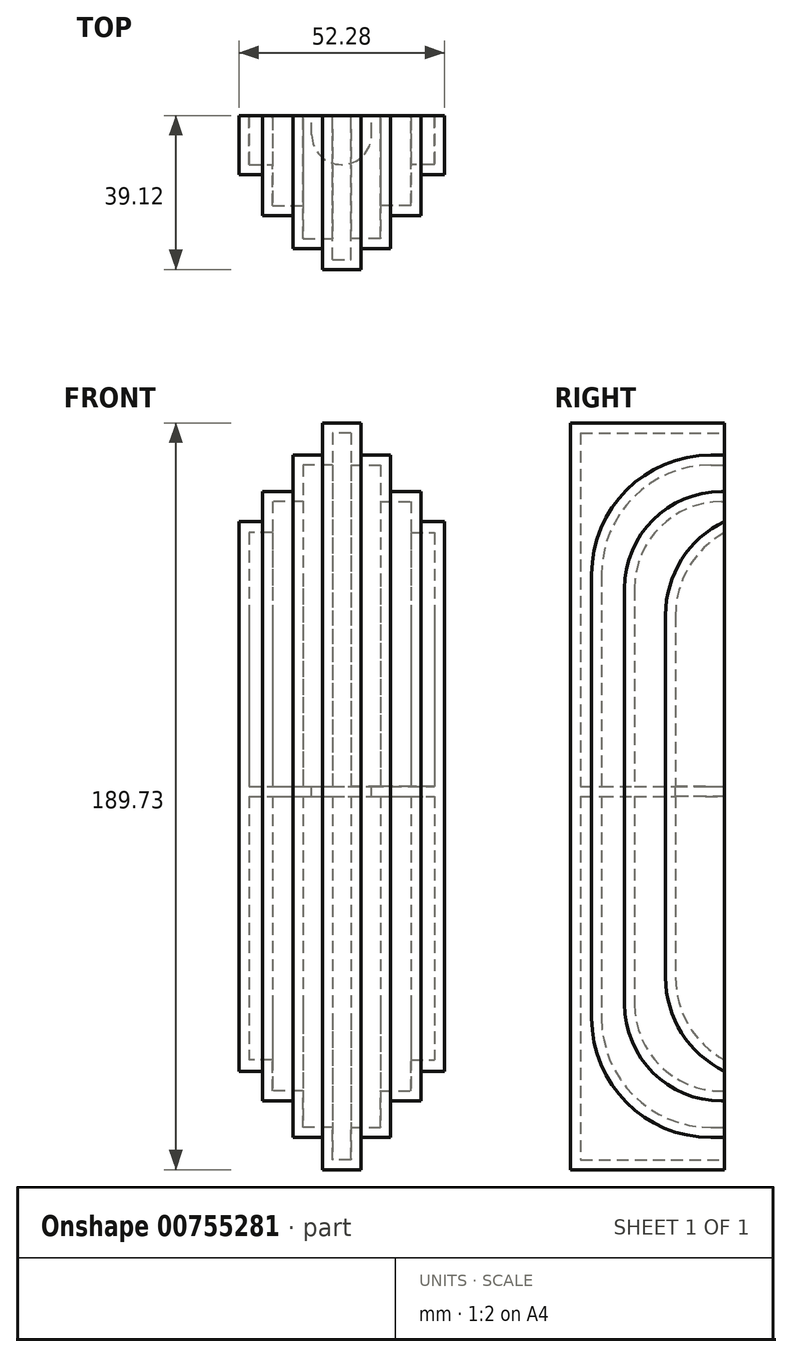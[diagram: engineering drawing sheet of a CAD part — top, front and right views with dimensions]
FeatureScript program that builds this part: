
annotation { "Feature Type Name" : "Feature", "Feature Type Description" : "" }
export const myFeature = defineFeature(function(context is Context, id is Id, definition is map)
    precondition{}
    {
        {
            var Q0;
            Q0=qCreatedBy(makeId("Front.planeOp"),FACE);
            var sketch = newSketch(context, id + "F0", { "sketchPlane" : qUnion([Q0])});
            skLineSegment(sketch, "E0", {"start": v(0, 33.47) * mm, "end": v(-4.86, 33.47) * mm});
            skLineSegment(sketch, "E1", {"start": v(-4.86, 33.47) * mm, "end": v(-4.86, -61.4) * mm});
            skLineSegment(sketch, "E2", {"start": v(-4.86, 25.31) * mm, "end": v(-12.33, 25.31) * mm});
            skLineSegment(sketch, "E3", {"start": v(-12.33, 25.31) * mm, "end": v(-12.33, -61.4) * mm});
            skLineSegment(sketch, "E4", {"start": v(-12.33, 16.06) * mm, "end": v(-20.13, 16.06) * mm});
            skLineSegment(sketch, "E5", {"start": v(-20.13, 16.06) * mm, "end": v(-20.13, -61.4) * mm});
            skLineSegment(sketch, "E6", {"start": v(-20.13, 8.45) * mm, "end": v(-26.14, 8.45) * mm});
            skLineSegment(sketch, "E7", {"start": v(-26.14, 8.45) * mm, "end": v(-26.14, -61.4) * mm});
            skPoint(sketch, "E8.start.orphan", {"position": v(-20.13, -61.4) * mm});
            skLineSegment(sketch, "E9", {"start": v(-26.14, -61.4) * mm, "end": v(-4.86, -61.4) * mm});
            skLineSegment(sketch, "E10.MirrorCS", {"start": v(0, 33.47) * mm, "end": v(4.86, 33.47) * mm});
            skLineSegment(sketch, "E11.MirrorCS", {"start": v(4.86, 33.47) * mm, "end": v(4.86, -61.4) * mm});
            skLineSegment(sketch, "E12.MirrorCS", {"start": v(4.86, 25.31) * mm, "end": v(12.33, 25.31) * mm});
            skLineSegment(sketch, "E13.MirrorCS", {"start": v(12.33, 16.06) * mm, "end": v(20.13, 16.06) * mm});
            skLineSegment(sketch, "E14.MirrorCS", {"start": v(12.33, 25.31) * mm, "end": v(12.33, -61.4) * mm});
            skLineSegment(sketch, "E15.MirrorCS", {"start": v(20.13, 8.45) * mm, "end": v(26.14, 8.45) * mm});
            skLineSegment(sketch, "E16.MirrorCS", {"start": v(26.14, 8.45) * mm, "end": v(26.14, -61.4) * mm});
            skLineSegment(sketch, "E17.MirrorCS", {"start": v(20.13, 16.06) * mm, "end": v(20.13, -61.4) * mm});
            skLineSegment(sketch, "E18.MirrorCS", {"start": v(26.14, -61.4) * mm, "end": v(4.86, -61.4) * mm});
            skLineSegment(sketch, "E19", {"start": v(-4.86, -61.4) * mm, "end": v(4.86, -61.4) * mm});
            skLineSegment(sketch, "E20.MirrorCS", {"start": v(-26.14, -131.24) * mm, "end": v(-26.14, -61.4) * mm});
            skLineSegment(sketch, "E21.MirrorCS", {"start": v(-20.13, -138.85) * mm, "end": v(-20.13, -61.4) * mm});
            skLineSegment(sketch, "E22.MirrorCS", {"start": v(-12.33, -148.1) * mm, "end": v(-12.33, -61.4) * mm});
            skLineSegment(sketch, "E23.MirrorCS", {"start": v(-4.86, -156.26) * mm, "end": v(-4.86, -61.4) * mm});
            skLineSegment(sketch, "E24.MirrorCS", {"start": v(4.86, -156.26) * mm, "end": v(4.86, -61.4) * mm});
            skLineSegment(sketch, "E25.MirrorCS", {"start": v(12.33, -148.1) * mm, "end": v(12.33, -61.4) * mm});
            skLineSegment(sketch, "E26.MirrorCS", {"start": v(20.13, -138.85) * mm, "end": v(20.13, -61.4) * mm});
            skLineSegment(sketch, "E27.MirrorCS", {"start": v(26.14, -131.24) * mm, "end": v(26.14, -61.4) * mm});
            skLineSegment(sketch, "E28.MirrorCS", {"start": v(12.33, -138.85) * mm, "end": v(20.13, -138.85) * mm});
            skLineSegment(sketch, "E29.MirrorCS", {"start": v(20.13, -131.24) * mm, "end": v(26.14, -131.24) * mm});
            skLineSegment(sketch, "E30.MirrorCS", {"start": v(4.86, -148.1) * mm, "end": v(12.33, -148.1) * mm});
            skLineSegment(sketch, "E31.MirrorCS", {"start": v(0, -156.26) * mm, "end": v(4.86, -156.26) * mm});
            skLineSegment(sketch, "E32.MirrorCS", {"start": v(0, -156.26) * mm, "end": v(-4.86, -156.26) * mm});
            skLineSegment(sketch, "E33.MirrorCS", {"start": v(-4.86, -148.1) * mm, "end": v(-12.33, -148.1) * mm});
            skLineSegment(sketch, "E34.MirrorCS", {"start": v(-12.33, -138.85) * mm, "end": v(-20.13, -138.85) * mm});
            skLineSegment(sketch, "E35.MirrorCS", {"start": v(-20.13, -131.24) * mm, "end": v(-26.14, -131.24) * mm});
            skSolve(sketch);
        }
        {
            var Q0;
            {var subQ4=sQuery(id+"F0.wireOp",EDGE,"E0");Q0=makeQuery(id+"F0.imprint","IMPRINT",FACE,{"disambiguationData":[TD([[makeQuery(id+"F0.imprint","IMPRINT",EDGE,{"derivedFrom":subQ4}),1.0]])]});}
            extrude(context, id + "F1", {"entities" : qUnion([Q0]), "depth" : 39.12 * mm, "offsetDistance" : 25.4 * mm});
        }
        {
            var Q0;
            {var subQ4=sQuery(id+"F0.wireOp",EDGE,"E2");Q0=makeQuery(id+"F0.imprint","IMPRINT",FACE,{"disambiguationData":[TD([[makeQuery(id+"F0.imprint","IMPRINT",EDGE,{"derivedFrom":subQ4}),1.0]])]});}
            extrude(context, id + "F2", {"entities" : qUnion([Q0]), "operationType" : NewBodyOperationType.ADD, "depth" : 33.78 * mm, "offsetDistance" : 25.4 * mm});
        }
        {
            var Q0;
            {var subQ4=sQuery(id+"F0.wireOp",EDGE,"E12.MirrorCS");Q0=makeQuery(id+"F0.imprint","IMPRINT",FACE,{"disambiguationData":[TD([[makeQuery(id+"F0.imprint","IMPRINT",EDGE,{"derivedFrom":subQ4}),-1.0]])]});}
            extrude(context, id + "F3", {"entities" : qUnion([Q0]), "operationType" : NewBodyOperationType.ADD, "depth" : 33.78 * mm, "offsetDistance" : 25.4 * mm});
        }
        {
            var Q0;
            {var subQ4=sQuery(id+"F0.wireOp",EDGE,"E4");Q0=makeQuery(id+"F0.imprint","IMPRINT",FACE,{"disambiguationData":[TD([[makeQuery(id+"F0.imprint","IMPRINT",EDGE,{"derivedFrom":subQ4}),1.0]])]});}
            extrude(context, id + "F4", {"entities" : qUnion([Q0]), "operationType" : NewBodyOperationType.ADD, "depth" : 25.4 * mm, "offsetDistance" : 25.4 * mm});
        }
        {
            var Q0;
            {var subQ5=sQuery(id+"F0.wireOp",EDGE,"E13.MirrorCS");Q0=makeQuery(id+"F0.imprint","IMPRINT",FACE,{"disambiguationData":[TD([[makeQuery(id+"F0.imprint","IMPRINT",EDGE,{"derivedFrom":subQ5}),-1.0]])]});}
            extrude(context, id + "F5", {"entities" : qUnion([Q0]), "operationType" : NewBodyOperationType.ADD, "depth" : 25.4 * mm, "offsetDistance" : 25.4 * mm});
        }
        {
            var Q0;
            {var subQ3=sQuery(id+"F0.wireOp",EDGE,"E6");Q0=makeQuery(id+"F0.imprint","IMPRINT",FACE,{"disambiguationData":[TD([[makeQuery(id+"F0.imprint","IMPRINT",EDGE,{"derivedFrom":subQ3}),1.0]])]});}
            extrude(context, id + "F6", {"entities" : qUnion([Q0]), "operationType" : NewBodyOperationType.ADD, "depth" : 15 * mm, "offsetDistance" : 25.4 * mm});
        }
        {
            var Q0;
            {var subQ0=sQuery(id+"F0.wireOp",EDGE,"E15.MirrorCS");Q0=makeQuery(id+"F0.imprint","IMPRINT",FACE,{"disambiguationData":[TD([[makeQuery(id+"F0.imprint","IMPRINT",EDGE,{"derivedFrom":subQ0}),-1.0]])]});}
            extrude(context, id + "F7", {"entities" : qUnion([Q0]), "operationType" : NewBodyOperationType.ADD, "depth" : 15 * mm, "offsetDistance" : 25.4 * mm});
        }
        {
            var Q0;
            Q0=makeQuery(id+"F7.opExtrude","CAP_EDGE",EDGE,{"disambiguationData":[OSD([sQuery(id+"F0.wireOp",EDGE,"E15.MirrorCS")])],"isStart":false});
            fillet(context, id + "F8", {"entities" : qUnion([Q0]), "radius" : 26.37 * mm, "tangentPropagation" : true, "allowEdgeOverflow" : false});
        }
        {
            var Q0;
            Q0=makeQuery(id+"F6.opExtrude","CAP_EDGE",EDGE,{"disambiguationData":[OSD([sQuery(id+"F0.wireOp",EDGE,"E6")])],"isStart":false});
            fillet(context, id + "F9", {"entities" : qUnion([Q0]), "radius" : 26.37 * mm, "tangentPropagation" : true, "allowEdgeOverflow" : false});
        }
        {
            var Q0;
            Q0=makeQuery(id+"F5.opExtrude","CAP_EDGE",EDGE,{"disambiguationData":[OSD([sQuery(id+"F0.wireOp",EDGE,"E13.MirrorCS")])],"isStart":false});
            fillet(context, id + "F10", {"entities" : qUnion([Q0]), "radius" : 24.65 * mm, "tangentPropagation" : true, "allowEdgeOverflow" : false});
        }
        {
            var Q0;
            Q0=makeQuery(id+"F4.opExtrude","CAP_EDGE",EDGE,{"disambiguationData":[OSD([sQuery(id+"F0.wireOp",EDGE,"E4")])],"isStart":false});
            fillet(context, id + "F11", {"entities" : qUnion([Q0]), "radius" : 24.66 * mm, "tangentPropagation" : true, "allowEdgeOverflow" : false});
        }
        {
            var Q0;
            Q0=makeQuery(id+"F2.opExtrude","CAP_EDGE",EDGE,{"disambiguationData":[OSD([sQuery(id+"F0.wireOp",EDGE,"E2")])],"isStart":false});
            fillet(context, id + "F12", {"entities" : qUnion([Q0]), "radius" : 30.35 * mm, "tangentPropagation" : true, "allowEdgeOverflow" : false});
        }
        {
            var Q0;
            Q0=makeQuery(id+"F3.opExtrude","CAP_EDGE",EDGE,{"disambiguationData":[OSD([sQuery(id+"F0.wireOp",EDGE,"E12.MirrorCS")])],"isStart":false});
            fillet(context, id + "F13", {"entities" : qUnion([Q0]), "radius" : 30.35 * mm, "tangentPropagation" : true, "allowEdgeOverflow" : false});
        }
        {
            var Q0;
            {var subQ0=sQuery(id+"F0.wireOp",EDGE,"E18.MirrorCS");var subQ1=sQuery(id+"F0.wireOp",EDGE,"E17.MirrorCS");var subQ2=sQuery(id+"F0.wireOp",EDGE,"E9");var subQ3=sQuery(id+"F0.wireOp",EDGE,"E5");var subQ4=sQuery(id+"F0.wireOp",EDGE,"E14.MirrorCS");var subQ5=sQuery(id+"F0.wireOp",EDGE,"E3");var subQ6=sQuery(id+"F0.wireOp",EDGE,"E11.MirrorCS");var subQ7=sQuery(id+"F0.wireOp",EDGE,"E1");Q0=makeQuery(id+"F7.boolean.opBoolean","MERGE",FACE,{"derivedFrom":[makeQuery(id+"F6.boolean.opBoolean","MERGE",FACE,{"derivedFrom":[makeQuery(id+"F5.boolean.opBoolean","MERGE",FACE,{"derivedFrom":[makeQuery(id+"F4.boolean.opBoolean","MERGE",FACE,{"derivedFrom":[makeQuery(id+"F3.boolean.opBoolean","MERGE",FACE,{"derivedFrom":[makeQuery(id+"F2.boolean.opBoolean","MERGE",FACE,{"derivedFrom":[makeQuery(id+"F1.opExtrude","CAP_FACE",FACE,{"disambiguationData":[OSD([sQuery(id+"F0.wireOp",EDGE,"E0"),subQ7,sQuery(id+"F0.wireOp",EDGE,"E10.MirrorCS"),subQ6,sQuery(id+"F0.wireOp",EDGE,"E19")])],"isStart":true}),makeQuery(id+"F2.opExtrude","CAP_FACE",FACE,{"disambiguationData":[OSD([subQ7,sQuery(id+"F0.wireOp",EDGE,"E2"),subQ5,subQ2])],"isStart":true})]}),makeQuery(id+"F3.opExtrude","CAP_FACE",FACE,{"disambiguationData":[OSD([subQ6,sQuery(id+"F0.wireOp",EDGE,"E12.MirrorCS"),subQ4,subQ0])],"isStart":true})]}),makeQuery(id+"F4.opExtrude","CAP_FACE",FACE,{"disambiguationData":[OSD([subQ5,sQuery(id+"F0.wireOp",EDGE,"E4"),subQ3,subQ2])],"isStart":true})]}),makeQuery(id+"F5.opExtrude","CAP_FACE",FACE,{"disambiguationData":[OSD([sQuery(id+"F0.wireOp",EDGE,"E13.MirrorCS"),subQ4,subQ1,subQ0])],"isStart":true})]}),makeQuery(id+"F6.opExtrude","CAP_FACE",FACE,{"disambiguationData":[OSD([subQ3,sQuery(id+"F0.wireOp",EDGE,"E6"),sQuery(id+"F0.wireOp",EDGE,"E7"),subQ2])],"isStart":true})]}),makeQuery(id+"F7.opExtrude","CAP_FACE",FACE,{"disambiguationData":[OSD([sQuery(id+"F0.wireOp",EDGE,"E15.MirrorCS"),sQuery(id+"F0.wireOp",EDGE,"E16.MirrorCS"),subQ1,subQ0])],"isStart":true})]});}
            shell(context, id + "F14", {"entities" : qUnion([Q0]), "thickness" : 2.54 * mm});
        }
        {
            var Q0;
            {var subQ3=sQuery(id+"F0.wireOp",EDGE,"E20.MirrorCS");Q0=makeQuery(id+"F0.imprint","IMPRINT",FACE,{"disambiguationData":[TD([[makeQuery(id+"F0.imprint","IMPRINT",EDGE,{"derivedFrom":subQ3}),-1.0]])]});}
            extrude(context, id + "F15", {"entities" : qUnion([Q0]), "operationType" : NewBodyOperationType.ADD, "depth" : 15 * mm, "offsetDistance" : 25.4 * mm});
        }
        {
            var Q0;
            Q0=makeQuery(id+"F15.opExtrude","CAP_EDGE",EDGE,{"disambiguationData":[OSD([sQuery(id+"F0.wireOp",EDGE,"E35.MirrorCS")])],"isStart":false});
            fillet(context, id + "F16", {"entities" : qUnion([Q0]), "radius" : 26.37 * mm, "tangentPropagation" : true, "allowEdgeOverflow" : false});
        }
        {
            var Q0;
            {var subQ3=sQuery(id+"F0.wireOp",EDGE,"E34.MirrorCS");Q0=makeQuery(id+"F0.imprint","IMPRINT",FACE,{"disambiguationData":[TD([[makeQuery(id+"F0.imprint","IMPRINT",EDGE,{"derivedFrom":subQ3}),-1.0]])]});}
            extrude(context, id + "F17", {"entities" : qUnion([Q0]), "operationType" : NewBodyOperationType.ADD, "depth" : 25.4 * mm, "offsetDistance" : 25.4 * mm});
        }
        {
            var Q0;
            Q0=makeQuery(id+"F17.opExtrude","CAP_EDGE",EDGE,{"disambiguationData":[OSD([sQuery(id+"F0.wireOp",EDGE,"E34.MirrorCS")])],"isStart":false});
            fillet(context, id + "F18", {"entities" : qUnion([Q0]), "radius" : 24.66 * mm, "tangentPropagation" : true, "allowEdgeOverflow" : false});
        }
        {
            var Q0;
            {var subQ3=sQuery(id+"F0.wireOp",EDGE,"E33.MirrorCS");Q0=makeQuery(id+"F0.imprint","IMPRINT",FACE,{"disambiguationData":[TD([[makeQuery(id+"F0.imprint","IMPRINT",EDGE,{"derivedFrom":subQ3}),-1.0]])]});}
            extrude(context, id + "F19", {"entities" : qUnion([Q0]), "operationType" : NewBodyOperationType.ADD, "depth" : 33.78 * mm, "offsetDistance" : 25.4 * mm});
        }
        {
            var Q0;
            Q0=makeQuery(id+"F19.opExtrude","CAP_EDGE",EDGE,{"disambiguationData":[OSD([sQuery(id+"F0.wireOp",EDGE,"E33.MirrorCS")])],"isStart":false});
            fillet(context, id + "F20", {"entities" : qUnion([Q0]), "radius" : 30.35 * mm, "tangentPropagation" : true, "allowEdgeOverflow" : false});
        }
        {
            var Q0;
            {var subQ4=sQuery(id+"F0.wireOp",EDGE,"E19");Q0=makeQuery(id+"F0.imprint","IMPRINT",FACE,{"disambiguationData":[TD([[makeQuery(id+"F0.imprint","IMPRINT",EDGE,{"derivedFrom":subQ4}),-1.0]])]});}
            extrude(context, id + "F21", {"entities" : qUnion([Q0]), "operationType" : NewBodyOperationType.ADD, "depth" : 39.12 * mm, "offsetDistance" : 25.4 * mm});
        }
        {
            var Q0;
            {var subQ6=sQuery(id+"F0.wireOp",EDGE,"E30.MirrorCS");Q0=makeQuery(id+"F0.imprint","IMPRINT",FACE,{"disambiguationData":[TD([[makeQuery(id+"F0.imprint","IMPRINT",EDGE,{"derivedFrom":subQ6}),1.0]])]});}
            extrude(context, id + "F22", {"entities" : qUnion([Q0]), "operationType" : NewBodyOperationType.ADD, "depth" : 33.78 * mm, "offsetDistance" : 25.4 * mm});
        }
        {
            var Q0;
            {var subQ4=sQuery(id+"F0.wireOp",EDGE,"E28.MirrorCS");Q0=makeQuery(id+"F0.imprint","IMPRINT",FACE,{"disambiguationData":[TD([[makeQuery(id+"F0.imprint","IMPRINT",EDGE,{"derivedFrom":subQ4}),1.0]])]});}
            extrude(context, id + "F23", {"entities" : qUnion([Q0]), "operationType" : NewBodyOperationType.ADD, "depth" : 25.4 * mm, "offsetDistance" : 25.4 * mm});
        }
        {
            var Q0;
            {var subQ4=sQuery(id+"F0.wireOp",EDGE,"E27.MirrorCS");Q0=makeQuery(id+"F0.imprint","IMPRINT",FACE,{"disambiguationData":[TD([[makeQuery(id+"F0.imprint","IMPRINT",EDGE,{"derivedFrom":subQ4}),1.0]])]});}
            extrude(context, id + "F24", {"entities" : qUnion([Q0]), "operationType" : NewBodyOperationType.ADD, "depth" : 15 * mm, "offsetDistance" : 25.4 * mm});
        }
        {
            var Q0;
            Q0=makeQuery(id+"F24.opExtrude","CAP_EDGE",EDGE,{"disambiguationData":[OSD([sQuery(id+"F0.wireOp",EDGE,"E29.MirrorCS")])],"isStart":false});
            fillet(context, id + "F25", {"entities" : qUnion([Q0]), "radius" : 26.37 * mm, "tangentPropagation" : true, "allowEdgeOverflow" : false});
        }
        {
            var Q0;
            Q0=makeQuery(id+"F23.opExtrude","CAP_EDGE",EDGE,{"disambiguationData":[OSD([sQuery(id+"F0.wireOp",EDGE,"E28.MirrorCS")])],"isStart":false});
            fillet(context, id + "F26", {"entities" : qUnion([Q0]), "radius" : 24.66 * mm, "tangentPropagation" : true, "allowEdgeOverflow" : false});
        }
        {
            var Q0;
            Q0=makeQuery(id+"F22.opExtrude","CAP_EDGE",EDGE,{"disambiguationData":[OSD([sQuery(id+"F0.wireOp",EDGE,"E30.MirrorCS")])],"isStart":false});
            fillet(context, id + "F27", {"entities" : qUnion([Q0]), "radius" : 30.35 * mm, "tangentPropagation" : true, "allowEdgeOverflow" : false});
        }
        {
            var Q0;
            {var subQ0=sQuery(id+"F0.wireOp",EDGE,"E18.MirrorCS");var subQ1=sQuery(id+"F0.wireOp",EDGE,"E26.MirrorCS");var subQ2=sQuery(id+"F0.wireOp",EDGE,"E25.MirrorCS");var subQ3=sQuery(id+"F0.wireOp",EDGE,"E24.MirrorCS");var subQ4=sQuery(id+"F0.wireOp",EDGE,"E23.MirrorCS");var subQ5=sQuery(id+"F0.wireOp",EDGE,"E19");var subQ6=sQuery(id+"F0.wireOp",EDGE,"E22.MirrorCS");var subQ7=sQuery(id+"F0.wireOp",EDGE,"E9");var subQ8=sQuery(id+"F0.wireOp",EDGE,"E21.MirrorCS");var subQ9=sQuery(id+"F0.wireOp",EDGE,"E17.MirrorCS");var subQ10=sQuery(id+"F0.wireOp",EDGE,"E5");var subQ11=sQuery(id+"F0.wireOp",EDGE,"E14.MirrorCS");var subQ12=sQuery(id+"F0.wireOp",EDGE,"E3");var subQ13=sQuery(id+"F0.wireOp",EDGE,"E11.MirrorCS");var subQ14=sQuery(id+"F0.wireOp",EDGE,"E1");Q0=makeQuery(id+"F24.boolean.opBoolean","MERGE",FACE,{"derivedFrom":[makeQuery(id+"F23.boolean.opBoolean","MERGE",FACE,{"derivedFrom":[makeQuery(id+"F22.boolean.opBoolean","MERGE",FACE,{"derivedFrom":[makeQuery(id+"F21.boolean.opBoolean","MERGE",FACE,{"derivedFrom":[makeQuery(id+"F19.boolean.opBoolean","MERGE",FACE,{"derivedFrom":[makeQuery(id+"F17.boolean.opBoolean","MERGE",FACE,{"derivedFrom":[makeQuery(id+"F15.boolean.opBoolean","MERGE",FACE,{"derivedFrom":[makeQuery(id+"F7.boolean.opBoolean","MERGE",FACE,{"derivedFrom":[makeQuery(id+"F6.boolean.opBoolean","MERGE",FACE,{"derivedFrom":[makeQuery(id+"F5.boolean.opBoolean","MERGE",FACE,{"derivedFrom":[makeQuery(id+"F4.boolean.opBoolean","MERGE",FACE,{"derivedFrom":[makeQuery(id+"F3.boolean.opBoolean","MERGE",FACE,{"derivedFrom":[makeQuery(id+"F2.boolean.opBoolean","MERGE",FACE,{"derivedFrom":[makeQuery(id+"F1.opExtrude","CAP_FACE",FACE,{"disambiguationData":[OSD([sQuery(id+"F0.wireOp",EDGE,"E0"),subQ14,sQuery(id+"F0.wireOp",EDGE,"E10.MirrorCS"),subQ13,subQ5])],"isStart":true}),makeQuery(id+"F2.opExtrude","CAP_FACE",FACE,{"disambiguationData":[OSD([subQ14,sQuery(id+"F0.wireOp",EDGE,"E2"),subQ12,subQ7])],"isStart":true})]}),makeQuery(id+"F3.opExtrude","CAP_FACE",FACE,{"disambiguationData":[OSD([subQ13,sQuery(id+"F0.wireOp",EDGE,"E12.MirrorCS"),subQ11,subQ0])],"isStart":true})]}),makeQuery(id+"F4.opExtrude","CAP_FACE",FACE,{"disambiguationData":[OSD([subQ12,sQuery(id+"F0.wireOp",EDGE,"E4"),subQ10,subQ7])],"isStart":true})]}),makeQuery(id+"F5.opExtrude","CAP_FACE",FACE,{"disambiguationData":[OSD([sQuery(id+"F0.wireOp",EDGE,"E13.MirrorCS"),subQ11,subQ9,subQ0])],"isStart":true})]}),makeQuery(id+"F6.opExtrude","CAP_FACE",FACE,{"disambiguationData":[OSD([subQ10,sQuery(id+"F0.wireOp",EDGE,"E6"),sQuery(id+"F0.wireOp",EDGE,"E7"),subQ7])],"isStart":true})]}),makeQuery(id+"F7.opExtrude","CAP_FACE",FACE,{"disambiguationData":[OSD([sQuery(id+"F0.wireOp",EDGE,"E15.MirrorCS"),sQuery(id+"F0.wireOp",EDGE,"E16.MirrorCS"),subQ9,subQ0])],"isStart":true})]}),makeQuery(id+"F15.opExtrude","CAP_FACE",FACE,{"disambiguationData":[OSD([subQ7,sQuery(id+"F0.wireOp",EDGE,"E20.MirrorCS"),subQ8,sQuery(id+"F0.wireOp",EDGE,"E35.MirrorCS")])],"isStart":true})]}),makeQuery(id+"F17.opExtrude","CAP_FACE",FACE,{"disambiguationData":[OSD([subQ7,subQ8,subQ6,sQuery(id+"F0.wireOp",EDGE,"E34.MirrorCS")])],"isStart":true})]}),makeQuery(id+"F19.opExtrude","CAP_FACE",FACE,{"disambiguationData":[OSD([subQ7,subQ6,subQ4,sQuery(id+"F0.wireOp",EDGE,"E33.MirrorCS")])],"isStart":true})]}),makeQuery(id+"F21.opExtrude","CAP_FACE",FACE,{"disambiguationData":[OSD([subQ5,subQ4,subQ3,sQuery(id+"F0.wireOp",EDGE,"E31.MirrorCS"),sQuery(id+"F0.wireOp",EDGE,"E32.MirrorCS")])],"isStart":true})]}),makeQuery(id+"F22.opExtrude","CAP_FACE",FACE,{"disambiguationData":[OSD([subQ3,subQ2,subQ0,sQuery(id+"F0.wireOp",EDGE,"E30.MirrorCS")])],"isStart":true})]}),makeQuery(id+"F23.opExtrude","CAP_FACE",FACE,{"disambiguationData":[OSD([subQ2,subQ1,subQ0,sQuery(id+"F0.wireOp",EDGE,"E28.MirrorCS")])],"isStart":true})]}),makeQuery(id+"F24.opExtrude","CAP_FACE",FACE,{"disambiguationData":[OSD([subQ1,sQuery(id+"F0.wireOp",EDGE,"E27.MirrorCS"),subQ0,sQuery(id+"F0.wireOp",EDGE,"E29.MirrorCS")])],"isStart":true})]});}
            shell(context, id + "F28", {"entities" : qUnion([Q0]), "thickness" : 2.54 * mm});
        }
        {
            var Q0;
            Q0=qCreatedBy(makeId("Top.planeOp"),FACE);
            var sketch = newSketch(context, id + "F29", { "sketchPlane" : qUnion([Q0])});
            skArc(sketch, "E36", {"start": v(-7.62, -4.86) * mm, "mid": v(0, -12.48) * mm, "end": v(7.62, -4.86) * mm});
            skLineSegment(sketch, "E37", {"start": v(-7.62, -4.86) * mm, "end": v(-7.62, 3.16) * mm});
            skLineSegment(sketch, "E38", {"start": v(7.62, -4.86) * mm, "end": v(7.62, 3.16) * mm});
            skLineSegment(sketch, "E39", {"start": v(7.62, 3.16) * mm, "end": v(-7.62, 3.16) * mm});
            skSolve(sketch);
        }
        {
            var Q0;
            Q0=makeQuery(id+"F29.imprint","IMPRINT",FACE,{"disambiguationData":[TD([[makeQuery(id+"F29.imprint","IMPRINT",EDGE,{"derivedFrom":sQuery(id+"F29.wireOp",EDGE,"E36")}),1.0]])]});
            extrude(context, id + "F30", {"entities" : qUnion([Q0]), "operationType" : NewBodyOperationType.REMOVE, "oppositeDirection" : true, "depth" : 81.8 * mm, "offsetDistance" : 25.4 * mm});
        }
    });
